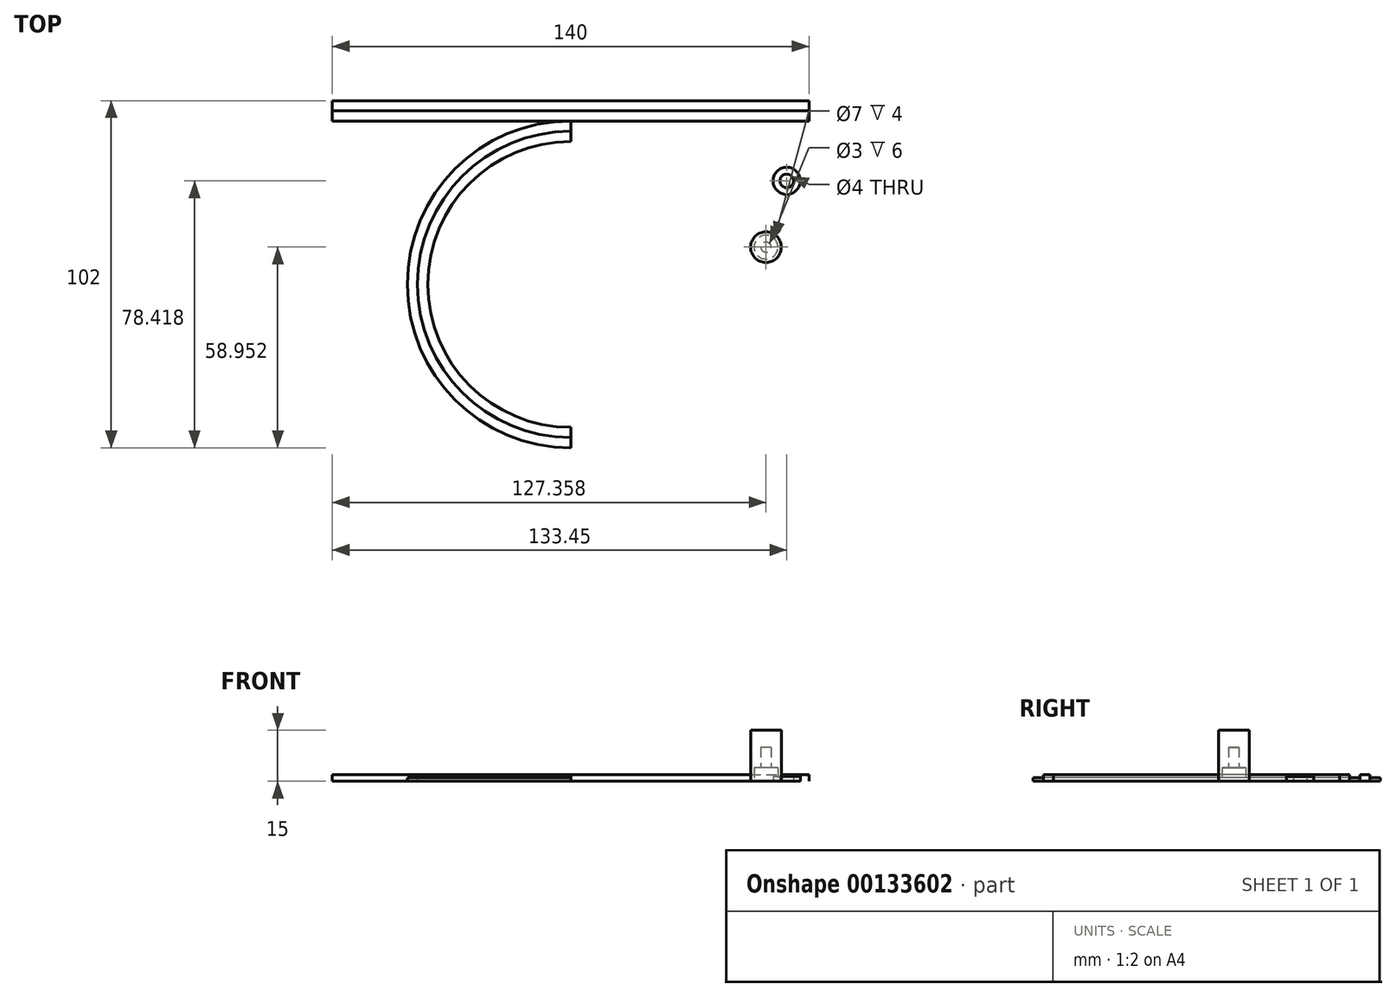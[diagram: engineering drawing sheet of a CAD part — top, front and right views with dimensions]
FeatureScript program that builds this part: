
annotation { "Feature Type Name" : "Feature", "Feature Type Description" : "" }
export const myFeature = defineFeature(function(context is Context, id is Id, definition is map)
    precondition{}
    {
        {
            var Q0;
            Q0=qCreatedBy(makeId("Top.planeOp"),FACE);
            var sketch = newSketch(context, id + "F0", { "sketchPlane" : qUnion([Q0])});
            skLineSegment(sketch, "E0", {"start": v(-70, 0) * mm, "end": v(70, 0) * mm});
            skLineSegment(sketch, "E1", {"start": v(70, 0) * mm, "end": v(70, 6) * mm});
            skLineSegment(sketch, "E2", {"start": v(70, 6) * mm, "end": v(-70, 6) * mm});
            skLineSegment(sketch, "E3", {"start": v(-70, 6) * mm, "end": v(-70, 0) * mm});
            skLineSegment(sketch, "E4.0", {"start": v(70, 3) * mm, "end": v(-70, 3) * mm});
            skLineSegment(sketch, "E5", {"start": v(0, 0) * mm, "end": v(0, -96) * mm, "construction": true});
            skArc(sketch, "E6", {"start": v(0, 0) * mm, "mid": v(-48, -48) * mm, "end": v(0, -96) * mm});
            skArc(sketch, "E7.0", {"start": v(0, -3) * mm, "mid": v(-45, -48) * mm, "end": v(0, -93) * mm});
            skArc(sketch, "E8.0", {"start": v(0, -6) * mm, "mid": v(-42, -48) * mm, "end": v(0, -90) * mm});
            skLineSegment(sketch, "E9", {"start": v(0, -6) * mm, "end": v(0, 0) * mm});
            skLineSegment(sketch, "E10", {"start": v(0, -90) * mm, "end": v(0, -96) * mm});
            skCircle(sketch, "E11", {"center": v(57.36, -37.05) * mm, "radius": 1.5 * mm});
            skCircle(sketch, "E12", {"center": v(63.45, -17.58) * mm, "radius": 2 * mm});
            skCircle(sketch, "E13", {"center": v(57.36, -37.05) * mm, "radius": 3.5 * mm});
            skCircle(sketch, "E14", {"center": v(57.36, -37.05) * mm, "radius": 4.5 * mm});
            skCircle(sketch, "E15", {"center": v(63.45, -17.58) * mm, "radius": 4 * mm});
            skSolve(sketch);
        }
        {
            var Q0;
            {var subQ3=sQuery(id+"F0.wireOp",EDGE,"E4.0");Q0=makeQuery(id+"F0.imprint","IMPRINT",FACE,{"disambiguationData":[TD([[makeQuery(id+"F0.imprint","IMPRINT",EDGE,{"derivedFrom":subQ3}),1.0]])]});}
            var Q1;
            {var subQ0=sQuery(id+"F0.wireOp",EDGE,"E7.0");Q1=makeQuery(id+"F0.imprint","IMPRINT",FACE,{"disambiguationData":[TD([[makeQuery(id+"F0.imprint","IMPRINT",EDGE,{"derivedFrom":subQ0}),1.0]])]});}
            extrude(context, id + "F1", {"entities" : qUnion([Q0, Q1]), "depth" : 2 * mm});
        }
        {
            var Q0;
            {var subQ0=sQuery(id+"F0.wireOp",EDGE,"E2");Q0=makeQuery(id+"F0.imprint","IMPRINT",FACE,{"disambiguationData":[TD([[makeQuery(id+"F0.imprint","IMPRINT",EDGE,{"derivedFrom":subQ0}),1.0]])]});}
            var Q1;
            {var subQ0=sQuery(id+"F0.wireOp",EDGE,"E6");Q1=makeQuery(id+"F0.imprint","IMPRINT",FACE,{"disambiguationData":[TD([[makeQuery(id+"F0.imprint","IMPRINT",EDGE,{"derivedFrom":subQ0}),1.0]])]});}
            extrude(context, id + "F2", {"entities" : qUnion([Q0, Q1]), "depth" : 1 * mm});
        }
        {
            var Q0;
            Q0=makeQuery(id+"F0.imprint","IMPRINT",FACE,{"disambiguationData":[TD([[makeQuery(id+"F0.imprint","IMPRINT",EDGE,{"derivedFrom":sQuery(id+"F0.wireOp",EDGE,"E12")}),-1.0]])]});
            extrude(context, id + "F3", {"entities" : qUnion([Q0]), "depth" : 1.5 * mm});
        }
        {
            var Q0;
            Q0=makeQuery(id+"F0.imprint","IMPRINT",FACE,{"disambiguationData":[TD([[makeQuery(id+"F0.imprint","IMPRINT",EDGE,{"derivedFrom":sQuery(id+"F0.wireOp",EDGE,"E13")}),-1.0]])]});
            var Q1;
            Q1=makeQuery(id+"F0.imprint","IMPRINT",FACE,{"disambiguationData":[TD([[makeQuery(id+"F0.imprint","IMPRINT",EDGE,{"derivedFrom":sQuery(id+"F0.wireOp",EDGE,"E11")}),-1.0]])]});
            var Q2;
            Q2=makeQuery(id+"F0.imprint","IMPRINT",FACE,{"disambiguationData":[TD([[makeQuery(id+"F0.imprint","IMPRINT",EDGE,{"derivedFrom":sQuery(id+"F0.wireOp",EDGE,"E11")}),1.0]])]});
            extrude(context, id + "F4", {"entities" : qUnion([Q0, Q1, Q2]), "depth" : 15 * mm});
        }
        {
            var Q0;
            Q0=makeQuery(id+"F0.imprint","IMPRINT",FACE,{"disambiguationData":[TD([[makeQuery(id+"F0.imprint","IMPRINT",EDGE,{"derivedFrom":sQuery(id+"F0.wireOp",EDGE,"E11")}),1.0]])]});
            extrude(context, id + "F5", {"entities" : qUnion([Q0]), "operationType" : NewBodyOperationType.REMOVE, "depth" : 10 * mm});
        }
        {
            var Q0;
            Q0=makeQuery(id+"F0.imprint","IMPRINT",FACE,{"disambiguationData":[TD([[makeQuery(id+"F0.imprint","IMPRINT",EDGE,{"derivedFrom":sQuery(id+"F0.wireOp",EDGE,"E11")}),-1.0]])]});
            extrude(context, id + "F6", {"entities" : qUnion([Q0]), "operationType" : NewBodyOperationType.REMOVE, "depth" : 4 * mm});
        }
    });
